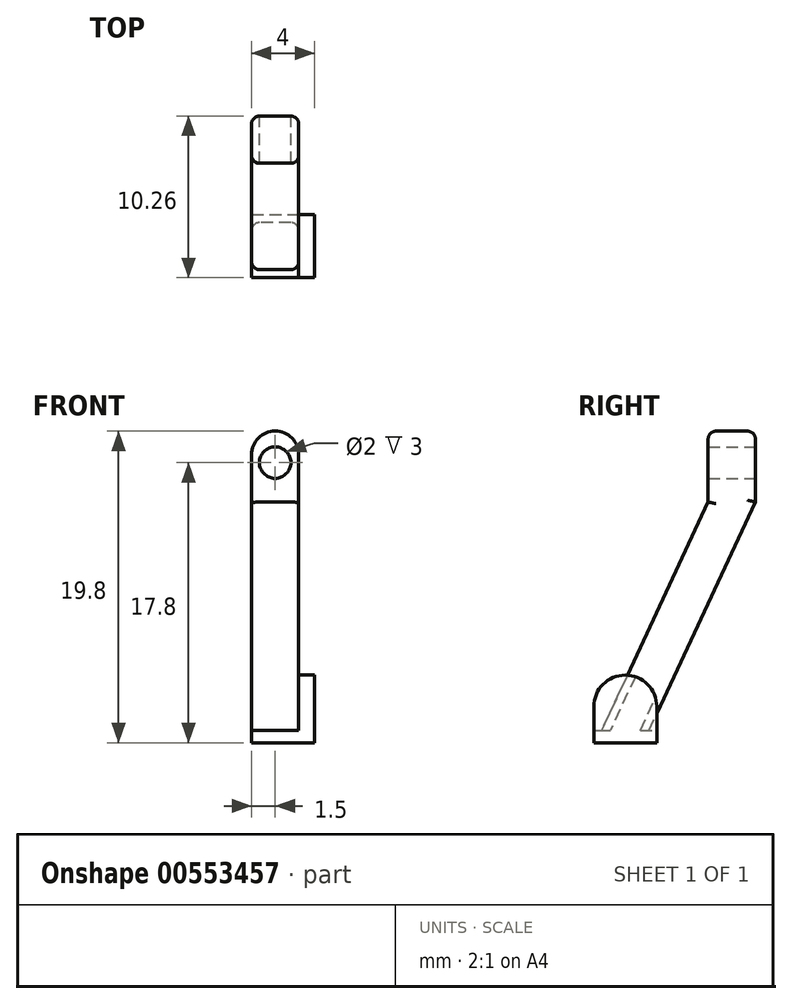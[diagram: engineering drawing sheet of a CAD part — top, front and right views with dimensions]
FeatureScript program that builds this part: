
annotation { "Feature Type Name" : "Feature", "Feature Type Description" : "" }
export const myFeature = defineFeature(function(context is Context, id is Id, definition is map)
    precondition{}
    {
        {
            var Q0;
            Q0=qCreatedBy(makeId("Top.planeOp"),FACE);
            var sketch = newSketch(context, id + "F0", { "sketchPlane" : qUnion([Q0])});
            skLineSegment(sketch, "E0.bottom", {"start": v(1, 0) * mm, "end": v(5, 0) * mm});
            skLineSegment(sketch, "E0.top", {"start": v(1, 4) * mm, "end": v(5, 4) * mm});
            skLineSegment(sketch, "E0.left", {"start": v(1, 0) * mm, "end": v(1, 4) * mm});
            skLineSegment(sketch, "E0.right", {"start": v(5, 0) * mm, "end": v(5, 4) * mm});
            skSolve(sketch);
        }
        {
            var Q0;
            Q0=qSketchRegion(id+"F0",true);
            extrude(context, id + "F1", {"entities" : qUnion([Q0]), "depth" : 0.8 * mm, "offsetDistance" : 25 * mm});
        }
        {
            var Q0;
            Q0=qCreatedBy(makeId("Right.planeOp"),FACE);
            cPlane(context, id + "F2", {"entities" : qUnion([Q0]), "cplaneType" : CPlaneType.OFFSET, "offset" : 2.5 * mm, "width" : 150 * mm, "height" : 150 * mm});
        }
        {
            var Q0;
            Q0=qCreatedBy(id+"F2.planeOp",FACE);
            var sketch = newSketch(context, id + "F3", { "sketchPlane" : qUnion([Q0])});
            skLineSegment(sketch, "E1", {"start": v(3.5, 0.8) * mm, "end": v(10.26, 15.3) * mm});
            skLineSegment(sketch, "E2", {"start": v(7.26, 15.3) * mm, "end": v(0.5, 0.8) * mm});
            skLineSegment(sketch, "E3", {"start": v(0.5, 0.8) * mm, "end": v(3.5, 0.8) * mm});
            skLineSegment(sketch, "E4", {"start": v(7.26, 15.3) * mm, "end": v(7.26, 19.8) * mm});
            skLineSegment(sketch, "E5", {"start": v(7.26, 19.8) * mm, "end": v(10.26, 19.8) * mm});
            skLineSegment(sketch, "E6", {"start": v(10.26, 19.8) * mm, "end": v(10.26, 15.3) * mm});
            skLineSegment(sketch, "E7", {"start": v(7.26, 15.3) * mm, "end": v(15, 15.3) * mm, "construction": true});
            skSolve(sketch);
        }
        {
            var Q0;
            Q0=qSketchRegion(id+"F3",true);
            extrude(context, id + "F4", {"entities" : qUnion([Q0]), "operationType" : NewBodyOperationType.ADD, "endBound" : BoundingType.SYMMETRIC, "depth" : 3 * mm, "offsetDistance" : 25 * mm});
        }
        {
            var Q0;
            Q0=makeQuery(id+"F4.opExtrude","SWEPT_FACE",FACE,{"disambiguationData":[OSD([sQuery(id+"F3.wireOp",EDGE,"E6")])]});
            var sketch = newSketch(context, id + "F5", { "sketchPlane" : qUnion([Q0])});
            skCircle(sketch, "E8", {"center": v(-2.5, 17.8) * mm, "radius": 1 * mm});
            skSolve(sketch);
        }
        {
            var Q0;
            Q0=qSketchRegion(id+"F5",true);
            extrude(context, id + "F6", {"entities" : qUnion([Q0]), "operationType" : NewBodyOperationType.REMOVE, "endBound" : BoundingType.THROUGH_ALL, "oppositeDirection" : true, "depth" : 25 * mm, "offsetDistance" : 25 * mm});
        }
        {
            var Q0;
            Q0=makeQuery(id+"F4.opExtrude","CAP_EDGE",EDGE,{"disambiguationData":[OSD([sQuery(id+"F3.wireOp",EDGE,"E5")])],"isStart":true});
            var Q1;
            Q1=makeQuery(id+"F4.opExtrude","CAP_EDGE",EDGE,{"disambiguationData":[OSD([sQuery(id+"F3.wireOp",EDGE,"E5")])],"isStart":false});
            fillet(context, id + "F7", {"entities" : qUnion([Q0, Q1]), "radius" : 1.5 * mm, "tangentPropagation" : true, "allowEdgeOverflow" : false});
        }
        {
            var Q0;
            Q0=makeQuery(id+"F4.opExtrude","CAP_EDGE",EDGE,{"disambiguationData":[OSD([sQuery(id+"F3.wireOp",EDGE,"E1")])],"isStart":true});
            var Q1;
            Q1=makeQuery(id+"F4.opExtrude","CAP_EDGE",EDGE,{"disambiguationData":[OSD([sQuery(id+"F3.wireOp",EDGE,"E6")])],"isStart":true});
            var Q2;
            Q2=makeQuery(id+"F7.opFillet","BLEND_EDGE",EDGE,{"blendedFrom":[makeQuery(id+"F4.opExtrude","CAP_EDGE",EDGE,{"disambiguationData":[OSD([sQuery(id+"F3.wireOp",EDGE,"E5")])],"isStart":false}),makeQuery(id+"F4.opExtrude","SWEPT_FACE",FACE,{"disambiguationData":[OSD([sQuery(id+"F3.wireOp",EDGE,"E6")])]})],"blendedInto":[makeQuery(id+"F4.opExtrude","SWEPT_FACE",FACE,{"disambiguationData":[OSD([sQuery(id+"F3.wireOp",EDGE,"E6")])]})]});
            var Q3;
            Q3=makeQuery(id+"F4.opExtrude","CAP_EDGE",EDGE,{"disambiguationData":[OSD([sQuery(id+"F3.wireOp",EDGE,"E1")])],"isStart":false});
            var Q4;
            Q4=makeQuery(id+"F4.opExtrude","CAP_EDGE",EDGE,{"disambiguationData":[OSD([sQuery(id+"F3.wireOp",EDGE,"E2")])],"isStart":true});
            var Q5;
            Q5=makeQuery(id+"F4.opExtrude","CAP_EDGE",EDGE,{"disambiguationData":[OSD([sQuery(id+"F3.wireOp",EDGE,"E4")])],"isStart":true});
            var Q6;
            Q6=makeQuery(id+"F4.opExtrude","CAP_EDGE",EDGE,{"disambiguationData":[OSD([sQuery(id+"F3.wireOp",EDGE,"E2")])],"isStart":false});
            fillet(context, id + "F8", {"entities" : qUnion([Q0, Q1, Q2, Q3, Q4, Q5, Q6]), "radius" : 0.5 * mm, "tangentPropagation" : true, "allowEdgeOverflow" : false});
        }
        {
            var Q0;
            Q0=makeQuery(id+"F1.opExtrude","SWEPT_FACE",FACE,{"disambiguationData":[OSD([sQuery(id+"F0.wireOp",EDGE,"E0.right")])]});
            var sketch = newSketch(context, id + "F9", { "sketchPlane" : qUnion([Q0])});
            skLineSegment(sketch, "E9.bottom", {"start": v(0, 0.8) * mm, "end": v(4, 0.8) * mm});
            skLineSegment(sketch, "E9.left", {"start": v(4, 0.8) * mm, "end": v(4, 2.3) * mm});
            skLineSegment(sketch, "E9.right", {"start": v(0, 0.8) * mm, "end": v(0, 2.3) * mm});
            skArc(sketch, "E10", {"start": v(4, 2.3) * mm, "mid": v(2, 4.3) * mm, "end": v(0, 2.3) * mm});
            skSolve(sketch);
        }
        {
            var Q0;
            Q0=qSketchRegion(id+"F9",true);
            extrude(context, id + "F10", {"entities" : qUnion([Q0]), "operationType" : NewBodyOperationType.ADD, "oppositeDirection" : true, "depth" : 1 * mm, "offsetDistance" : 25 * mm});
        }
    });
